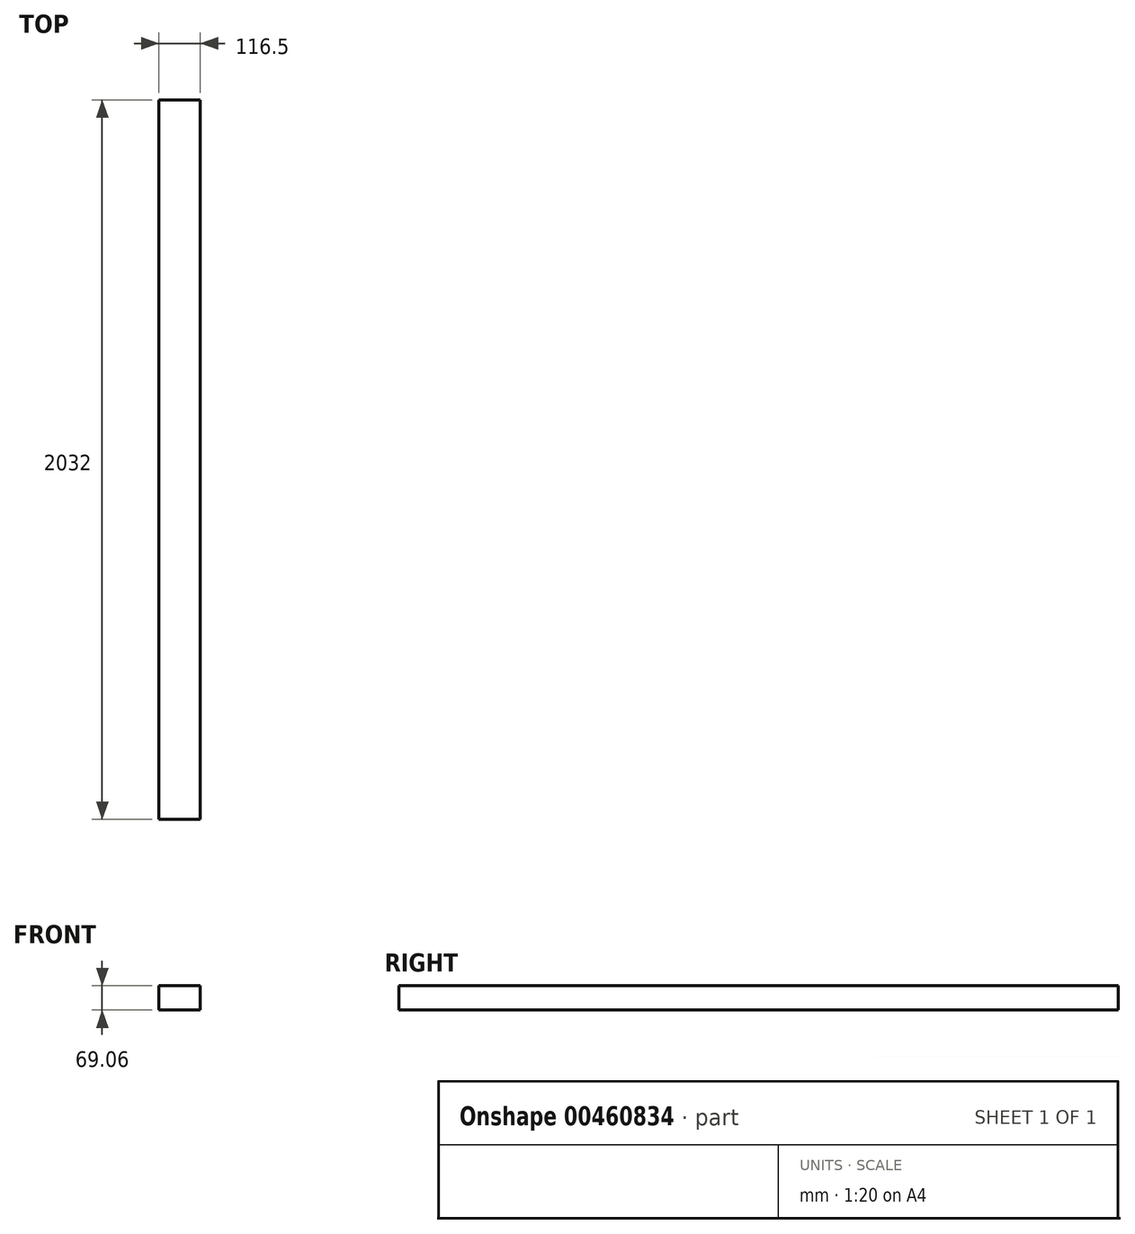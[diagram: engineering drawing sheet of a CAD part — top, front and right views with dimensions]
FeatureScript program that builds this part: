
annotation { "Feature Type Name" : "Feature", "Feature Type Description" : "" }
export const myFeature = defineFeature(function(context is Context, id is Id, definition is map)
    precondition{}
    {
        {
            var Q0;
            Q0=qCreatedBy(makeId("Front.planeOp"),FACE);
            var sketch = newSketch(context, id + "F0", { "sketchPlane" : qUnion([Q0])});
            skLineSegment(sketch, "E0.bottom", {"start": v(58.25, -34.53) * mm, "end": v(-58.25, -34.53) * mm});
            skLineSegment(sketch, "E0.top", {"start": v(58.25, 34.53) * mm, "end": v(-58.25, 34.53) * mm});
            skLineSegment(sketch, "E0.left", {"start": v(58.25, -34.53) * mm, "end": v(58.25, 34.53) * mm});
            skLineSegment(sketch, "E0.right", {"start": v(-58.25, -34.53) * mm, "end": v(-58.25, 34.53) * mm});
            skPoint(sketch, "E0.middle", {"position": v(0, 0) * mm});
            skSolve(sketch);
        }
        {
            var Q0;
            Q0 = qSketchRegion(id + "F0", true);
            extrude(context, id + "F1", {"entities" : qUnion([Q0]), "depth" : 2032 * mm});
        }
    });
